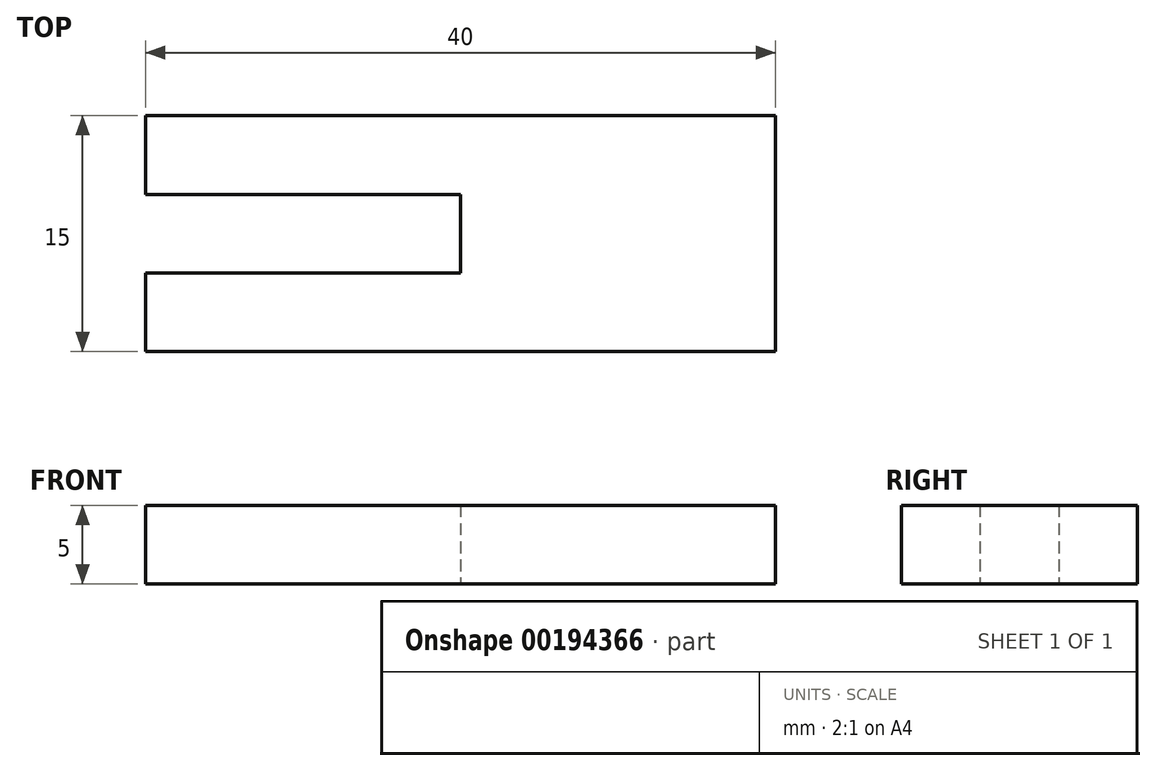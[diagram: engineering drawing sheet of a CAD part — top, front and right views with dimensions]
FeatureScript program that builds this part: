
annotation { "Feature Type Name" : "Feature", "Feature Type Description" : "" }
export const myFeature = defineFeature(function(context is Context, id is Id, definition is map)
    precondition{}
    {
        {
            var Q0;
            Q0=qCreatedBy(makeId("Top.planeOp"),FACE);
            var sketch = newSketch(context, id + "F0", { "sketchPlane" : qUnion([Q0])});
            skLineSegment(sketch, "E0.bottom", {"start": v(-20, 7.5) * mm, "end": v(20, 7.5) * mm});
            skLineSegment(sketch, "E0.top", {"start": v(-20, -7.5) * mm, "end": v(20, -7.5) * mm});
            skLineSegment(sketch, "E0.right", {"start": v(20, 7.5) * mm, "end": v(20, -7.5) * mm});
            skPoint(sketch, "E0.middle", {"position": v(0, 0) * mm});
            skLineSegment(sketch, "E1.bottom", {"start": v(-20, 2.5) * mm, "end": v(0, 2.5) * mm});
            skLineSegment(sketch, "E1.top", {"start": v(-20, -2.5) * mm, "end": v(0, -2.5) * mm});
            skLineSegment(sketch, "E1.right", {"start": v(0, 2.5) * mm, "end": v(0, -2.5) * mm});
            skLineSegment(sketch, "E2.trimOffspring", {"start": v(-20, -2.5) * mm, "end": v(-20, -7.5) * mm});
            skLineSegment(sketch, "E3", {"start": v(-20, 7.5) * mm, "end": v(-20, 2.5) * mm});
            skSolve(sketch);
        }
        {
            var Q0;
            Q0 = qSketchRegion(id + "F0", true);
            extrude(context, id + "F1", {"entities" : qUnion([Q0]), "depth" : 5 * mm});
        }
    });
